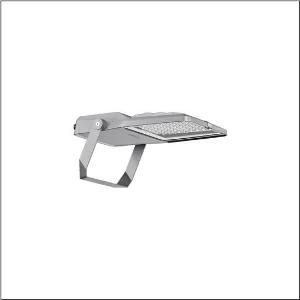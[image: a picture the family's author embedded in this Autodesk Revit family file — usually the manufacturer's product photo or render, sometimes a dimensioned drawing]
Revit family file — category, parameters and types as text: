
# Revit family: floodlight_fl_21_iq_mini___pl43_5xa7772b4a1a_cc8f
name_source: partatom
category: Lighting Fixtures
units: mm (PartAtom-declared; Revit-internal decimal feet)

## family parameters
Cut with Voids When Loaded = No
Host = Face
Light Source = No
Part Type = Normal
Room Calculation Point = No
Round Connector Dimension = Use Diameter
Shared = No

## types (1)
- --- (1 x LED, 6660 lm, 45.5 W, 4000K)
    Apparent Load = 46 VA
    CIE Flux Codes = 27 78 99 100 100
    Color Rendering = 70
    Color Temperature = 4000K
    Default Elevation = 1800 mm
    Description = Floodlight FL 21 iQ mini, floodlight, primary light control with lens, of PMMA, primary optical cover: protective disc, of toughened safety glass, transparent, light distribution: PL43, light emission: direct distribution, installation type: surface-mounted, LED, High Power LED, rated luminous flux: 6.660lm, luminous efficacy: 146lm/W, light colour: 740, colour temperature: 4000K, control: Street-Remote, Auto-Match, Temp-Guard, Night-Set, Smart-Wire, Desk-Remote (wireless, voltage-free reading and setting of iQ features in the workshop via application-optimized NFC function/RFID function), optimised constant luminous flux control (CLO 2.0), with terminal, 6-pole, mains connection: 220..240V, AC, 50/60Hz, start of lifetime: 46W, end of service life: 48W, reduction: 22W, luminaire housing, of diecast aluminium, powder-coated, Siteco® metallic grey (DB 702S), corrosivity category C5 mid according to DIN EN ISO 12944, sealing non-destructively replaceable, mounting bracket, of steel, galvanised, powder-coated, Siteco® metallic grey (DB 702S), protection rating (complete): IP66, insulation class (complete): insulation class II (safety insulation), certification: CE, ENEC, VDE, protection symbol: D, impact resistance: IK08, permissible operating ambient temperature: -40..+40°C, permissible operating ambient temperature for outdoor applications: -40..+50°C, standard: DIN EN 12944, LABS conformity tested according to VDMA 24364:2018-05, packaging unit: 1 piece

Light Distribution: PL43
    Height = 70 mm
    Lamp = 1 x LED
    Lamp Light Flux = 6660 lm
    Lamp Power = 45.5 W
    Lamp count = 1
    Length = 485 mm
    Luminous efficacy = 146 lm/W
    Manufacturer = Siteco
    ModVariant = No
    Model = 5XA7772B4A1A
    Number of Poles = 1
    OnlyDefault = Yes
    Power Factor = 1
    Product Name = Floodlight FL 21 iQ mini | PL43
    Product group = floodlight | pylon annexe
    ProductGroupID = 6200
    Protection Class = Protection class II
    Protection Degree = IP 66
    RLX_Detail_Level = 1
    RLX_Emergency_Light_Flux = 0 lm
    RLX_Emergency_Type = 0
    RLX_Emergency_Type_DB = No
    RlxData = <blob elided: 95893 chars, md5=60f47275>
    Socket = socket
    Standby Power = 0 W
    System Light Flux = 6660 lm
    System Power = 46 W
    Type Comments = factory setting: luminous flux: 100 % | dim-lin: 254 | 463 mA
    Type Image = l_1006845.jpg
    URL = http://relux.com
    VarID = @adj_094277
    Voltage = 0 V
    Weight = 0.00 kg
    Width = 337 mm

## geometry (parser evidence)
native form markers: Blend x4, Sweep x12
no freeform markers — native parametric forms only
